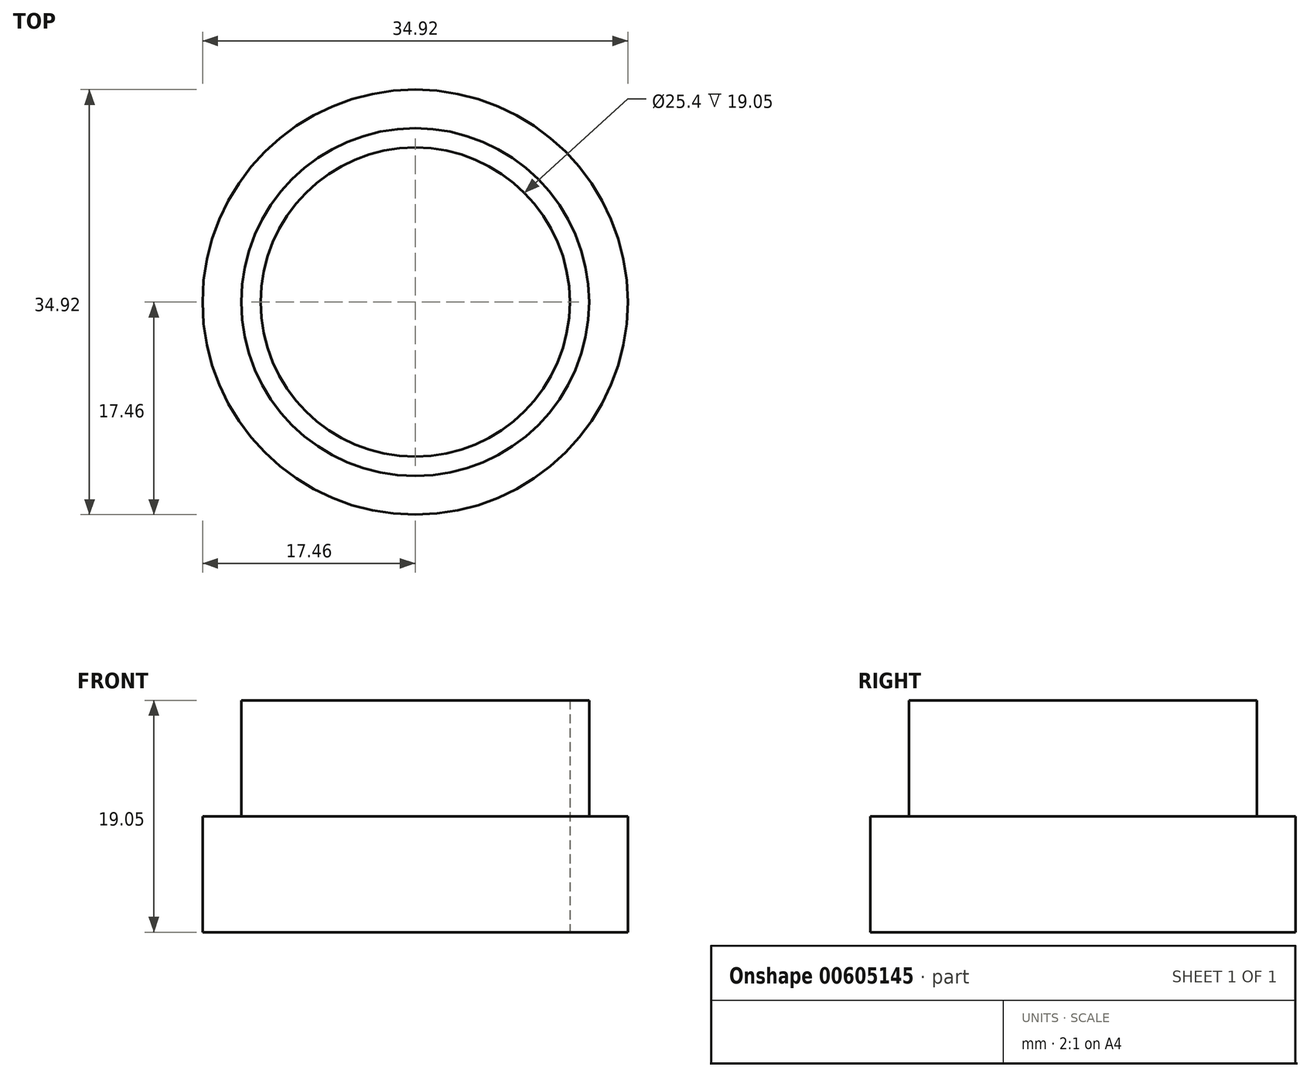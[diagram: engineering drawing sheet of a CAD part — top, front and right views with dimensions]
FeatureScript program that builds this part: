
annotation { "Feature Type Name" : "Feature", "Feature Type Description" : "" }
export const myFeature = defineFeature(function(context is Context, id is Id, definition is map)
    precondition{}
    {
        {
            var Q0;
            Q0=qCreatedBy(makeId("Top.planeOp"),FACE);
            var sketch = newSketch(context, id + "F0", { "sketchPlane" : qUnion([Q0])});
            skLineSegment(sketch, "E0", {"start": v(0, 0) * mm, "end": v(12.7, 0) * mm});
            skCircle(sketch, "E1", {"center": v(0, 0) * mm, "radius": 12.7 * mm});
            skCircle(sketch, "E2.0", {"center": v(0, 0) * mm, "radius": 14.29 * mm});
            skSolve(sketch);
        }
        {
            var Q0;
            Q0=qCreatedBy(makeId("Top.planeOp"),FACE);
            var sketch = newSketch(context, id + "F1", { "sketchPlane" : qUnion([Q0])});
            skSolve(sketch);
        }
        {
            var Q0;
            Q0=qSketchRegion(id+"F1",true);
            var Q1;
            Q1=makeQuery(id+"F0.imprint","IMPRINT",FACE,{"disambiguationData":[TD([[makeQuery(id+"F0.imprint","IMPRINT",EDGE,{"derivedFrom":sQuery(id+"F0.wireOp",EDGE,"E1")}),-1.0]])]});
            extrude(context, id + "F2", {"entities" : qUnion([Q0, Q1]), "depth" : 19.05 * mm, "offsetDistance" : 25.4 * mm});
        }
        {
            var Q0;
            Q0=qSketchRegion(id+"F0",true);
            var sketch = newSketch(context, id + "F3", { "sketchPlane" : qUnion([Q0])});
            skCircle(sketch, "E3.0", {"center": v(0, 0) * mm, "radius": 17.46 * mm});
            skSolve(sketch);
        }
        {
            var Q0;
            Q0=makeQuery(id+"F3.imprint","IMPRINT",FACE,{"disambiguationData":[TD([[makeQuery(id+"F3.imprint","IMPRINT",EDGE,{"derivedFrom":sQuery(id+"F3.wireOp",EDGE,"E3.0")}),1.0]])]});
            var Q1;
            Q1=sQuery(id+"F3.wireOp",EDGE,"E3.0");
            var Q2;
            Q2=sQuery(id+"F0.wireOp",EDGE,"E2.0");
            extrude(context, id + "F4", {"entities" : qUnion([Q0]), "operationType" : NewBodyOperationType.ADD, "surfaceEntities" : qUnion([Q1, Q2]), "depth" : 9.52 * mm, "offsetDistance" : 25.4 * mm});
        }
    });
